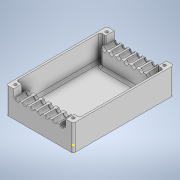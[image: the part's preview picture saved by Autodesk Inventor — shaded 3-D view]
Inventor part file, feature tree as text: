
AUTODESK INVENTOR PART (.ipt)
format: ipt  version: 2021 (Build 250183000, 183)  size: 503,296 bytes
history: native  units: mm
features: sketch x12, extrude x11, fillet x3, projected_geometry x1
ambient origin geometry x8: Origin, YZ Plane, XZ Plane, XY Plane, X Axis, Y Axis, Z Axis, Center Point
bodies: Body1 (feature_tree)
feature tree (27):
  extrude  "Extrusion20"  Depth=108.0mm
  extrude  "Extrusion21"  Depth=2.0mm TaperAngle=0.0deg
  extrude  "Extrusion24"  Depth=20.0mm TaperAngle=0.0deg
  fillet  "Fillet12"  Radius=3.0mm
  extrude  "Extrusion25"  Depth=3.0mm
  fillet  "Fillet13"  Radius=3.0mm
  extrude  "Extrusion26"  Depth=2.0mm
  extrude  "Extrusion27"  Depth=56.0mm
  extrude  "Extrusion28"  Depth=15.0mm
  extrude  "Extrusion29"  Depth=15.0mm
  extrude  "Extrusion30"  Depth=2.0mm
  sketch  "Sketch37"  dims[d308=56.0mm d309=15.0mm]
  extrude  "Extrusion31"  Depth=15.0mm
  extrude  "Extrusion32"  Depth=12.0mm TaperAngle=0.0deg
  fillet  "Fillet17"  Radius=6.0mm
  sketch  "Sketch26"  dims[d181=2.0mm d182=2.0mm d184=2.0mm d186=2.0mm d187=8.0mm d190=8.0mm d193=8.0mm d196=8.0mm d249=108.0mm]
  sketch  "Sketch27"  dims[d250=72.0mm d251=2.0mm d252=0.0mm]
  sketch  "Sketch30"  dims[d253=2.0mm d254=20.0mm d255=0.0mm d292=3.0mm]
  sketch  "Sketch31"  dims[d293=3.0mm d294=3.0mm d295=3.0mm]
  sketch  "Sketch32"  dims[d296=20.0mm d297=0.0mm d298=2.0mm]
  sketch  "Sketch33"  dims[d299=56.0mm d300=56.0mm]
  sketch  "Sketch34"  dims[d301=8.0mm d302=15.0mm]
  sketch  "Sketch35"  dims[d303=8.0mm d304=15.0mm]
  sketch  "Sketch36"  dims[d305=8.0mm d306=0.0mm d307=2.0mm]
  sketch  "Sketch38"  dims[d310=15.0mm d311=12.0mm d312=0.0mm d313=6.0mm]
  projected_geometry  "Projected Loop1"
  sketch  "Sketch39"  dims[d314=4.0mm d315=70.0mm d317=8.0mm d318=10.0mm d320=10.0mm d322=1000.0mm d323=0.0mm d324=1.0mm d325=1.0mm d326=3.0mm d327=3.0mm d328=8.0mm d329=0.0mm d330=4.0mm d331=4.5mm d332=70.0mm d334=8.0mm d335=10.0mm d337=10.0mm d339=1000.0mm d340=0.0mm d344=5.0mm d345=5.0mm d346=5.0mm d347=5.0mm d348=5.0mm d349=5.0mm d350=5.0mm d351=5.0mm d352=2.0mm d353=10000.0mm d354=0.0mm d355=6.0mm d356=0.0mm d357=2.0mm d358=0.0mm d359=2.5mm]
